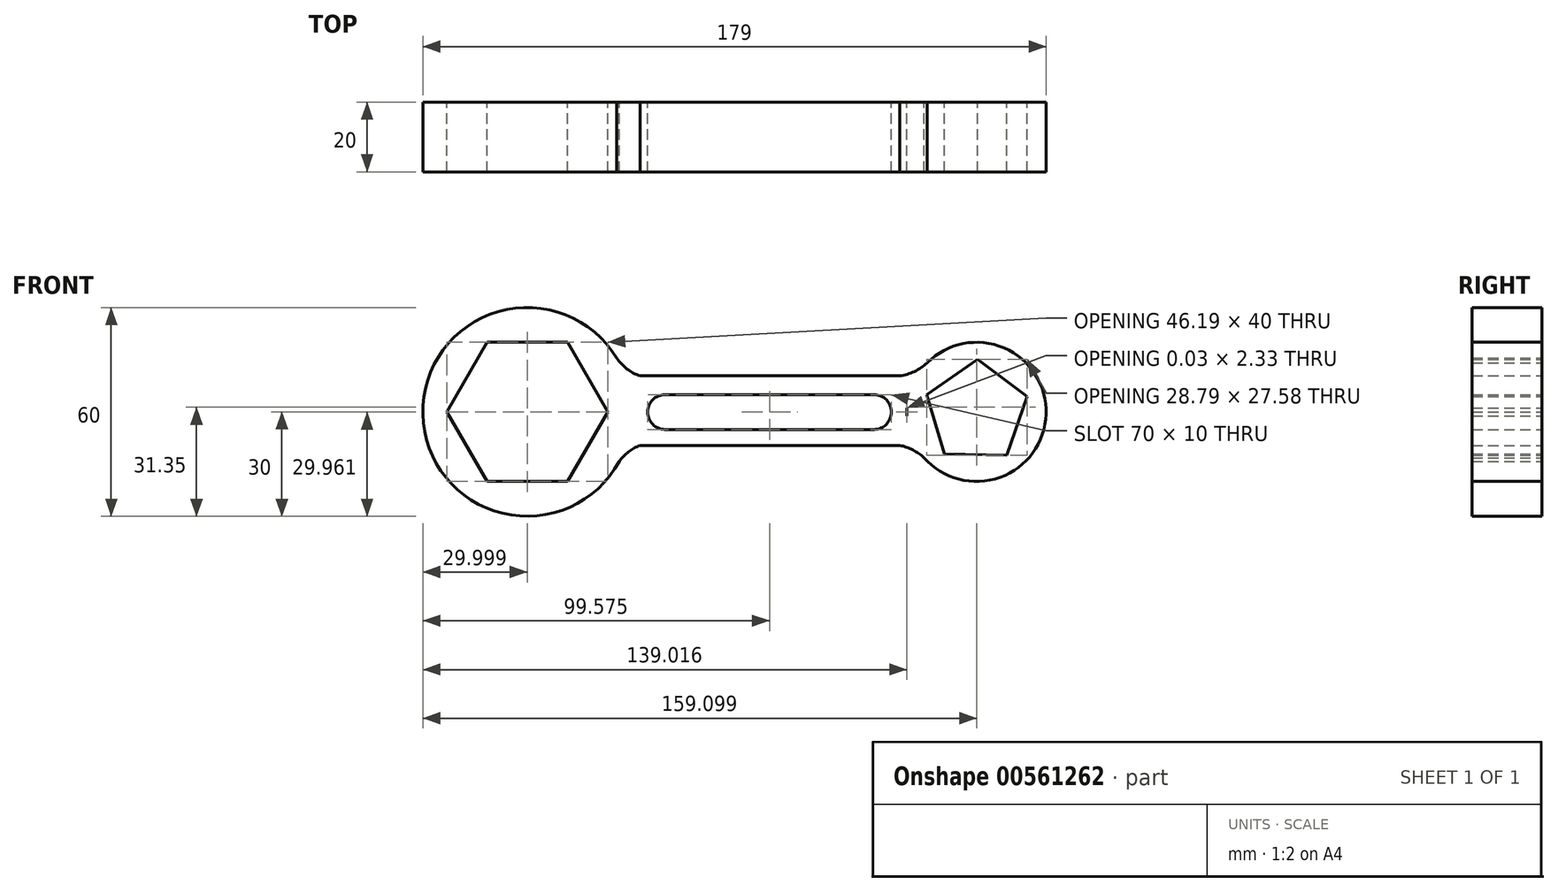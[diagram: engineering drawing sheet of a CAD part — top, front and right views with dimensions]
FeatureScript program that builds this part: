
annotation { "Feature Type Name" : "Feature", "Feature Type Description" : "" }
export const myFeature = defineFeature(function(context is Context, id is Id, definition is map)
    precondition{}
    {
        {
            var Q0;
            Q0=qCreatedBy(makeId("Front.planeOp"),FACE);
            var sketch = newSketch(context, id + "F0", { "sketchPlane" : qUnion([Q0])});
            skCircle(sketch, "E0.cCircle", {"center": v(-57.95, -20) * mm, "radius": 20 * mm, "construction": true});
            skLineSegment(sketch, "E0.0", {"start": v(-69.5, 0) * mm, "end": v(-46.4, 0) * mm});
            skLineSegment(sketch, "E0.1", {"start": v(-46.4, 0) * mm, "end": v(-34.86, -20) * mm});
            skLineSegment(sketch, "E0.2", {"start": v(-34.86, -20) * mm, "end": v(-46.4, -40) * mm});
            skLineSegment(sketch, "E0.3", {"start": v(-46.4, -40) * mm, "end": v(-69.5, -40) * mm});
            skLineSegment(sketch, "E0.4", {"start": v(-69.5, -40) * mm, "end": v(-81.05, -20) * mm});
            skLineSegment(sketch, "E0.5", {"start": v(-81.05, -20) * mm, "end": v(-69.5, 0) * mm});
            skPoint(sketch, "E0.0.midPoint", {"position": v(-57.95, 0) * mm});
            skCircle(sketch, "E1.cCircle", {"center": v(71.05, -20) * mm, "radius": 12.25 * mm, "construction": true});
            skLineSegment(sketch, "E1.0", {"start": v(56.75, -15.01) * mm, "end": v(71.37, -4.86) * mm});
            skLineSegment(sketch, "E1.1", {"start": v(71.37, -4.86) * mm, "end": v(85.55, -15.63) * mm});
            skLineSegment(sketch, "E1.2", {"start": v(85.55, -15.63) * mm, "end": v(79.68, -32.44) * mm});
            skLineSegment(sketch, "E1.3", {"start": v(79.68, -32.44) * mm, "end": v(61.89, -32.06) * mm});
            skLineSegment(sketch, "E1.4", {"start": v(61.89, -32.06) * mm, "end": v(56.75, -15.01) * mm});
            skPoint(sketch, "E1.0.midPoint", {"position": v(64.06, -9.94) * mm});
            skCircle(sketch, "E2", {"center": v(-57.95, -20) * mm, "radius": 30 * mm});
            skCircle(sketch, "E3", {"center": v(71.05, -20) * mm, "radius": 20 * mm});
            skLineSegment(sketch, "E4.bottom", {"start": v(-25.54, -9.64) * mm, "end": v(49.03, -9.64) * mm});
            skLineSegment(sketch, "E4.top", {"start": v(-25.54, -29.64) * mm, "end": v(49.03, -29.64) * mm});
            skLineSegment(sketch, "E4.right", {"start": v(51.08, -18.83) * mm, "end": v(51.08, -21.17) * mm});
            skLineSegment(sketch, "E5.bottom", {"start": v(-18.38, -15.04) * mm, "end": v(41.62, -15.04) * mm});
            skLineSegment(sketch, "E5.top", {"start": v(-18.38, -25.04) * mm, "end": v(41.62, -25.04) * mm});
            skLineSegment(sketch, "E5.left", {"start": v(-23.38, -20.04) * mm, "end": v(-23.38, -20.04) * mm});
            skLineSegment(sketch, "E5.right", {"start": v(46.62, -20.04) * mm, "end": v(46.62, -20.04) * mm});
            skPoint(sketch, "E6.visualSharp", {"position": v(-23.38, -15.04) * mm});
            skArc(sketch, "E6.filletArc", {"start": v(-18.38, -15.04) * mm, "mid": v(-21.91, -16.5) * mm, "end": v(-23.38, -20.04) * mm});
            skPoint(sketch, "E7.visualSharp", {"position": v(-23.38, -25.04) * mm});
            skArc(sketch, "E7.filletArc", {"start": v(-23.38, -20.04) * mm, "mid": v(-21.91, -23.57) * mm, "end": v(-18.38, -25.04) * mm});
            skPoint(sketch, "E8.visualSharp", {"position": v(46.62, -15.04) * mm});
            skArc(sketch, "E8.filletArc", {"start": v(46.62, -20.04) * mm, "mid": v(45.16, -16.5) * mm, "end": v(41.62, -15.04) * mm});
            skPoint(sketch, "E9.visualSharp", {"position": v(46.62, -25.04) * mm});
            skArc(sketch, "E9.filletArc", {"start": v(41.62, -25.04) * mm, "mid": v(45.16, -23.57) * mm, "end": v(46.62, -20.04) * mm});
            skArc(sketch, "E10", {"start": v(-25.54, -29.64) * mm, "mid": v(-28.9, -31.5) * mm, "end": v(-31.56, -34.27) * mm});
            skArc(sketch, "E11", {"start": v(-32.22, -4.57) * mm, "mid": v(-29.3, -7.66) * mm, "end": v(-25.54, -9.64) * mm});
            skArc(sketch, "E12", {"start": v(56, -33.18) * mm, "mid": v(52.77, -30.92) * mm, "end": v(49.03, -29.64) * mm});
            skArc(sketch, "E13", {"start": v(49.03, -9.64) * mm, "mid": v(53.23, -8.4) * mm, "end": v(56.85, -5.92) * mm});
            skPoint(sketch, "E14.end.orphan", {"position": v(53.53, -29.64) * mm});
            skPoint(sketch, "E15.end.orphan", {"position": v(-29.54, -29.64) * mm});
            skSolve(sketch);
        }
        {
            var Q0;
            Q0 = qSketchRegion(id + "F0", true);
            extrude(context, id + "F1", {"entities" : qUnion([Q0]), "depth" : 20 * mm, "offsetDistance" : 25 * mm});
        }
    });
